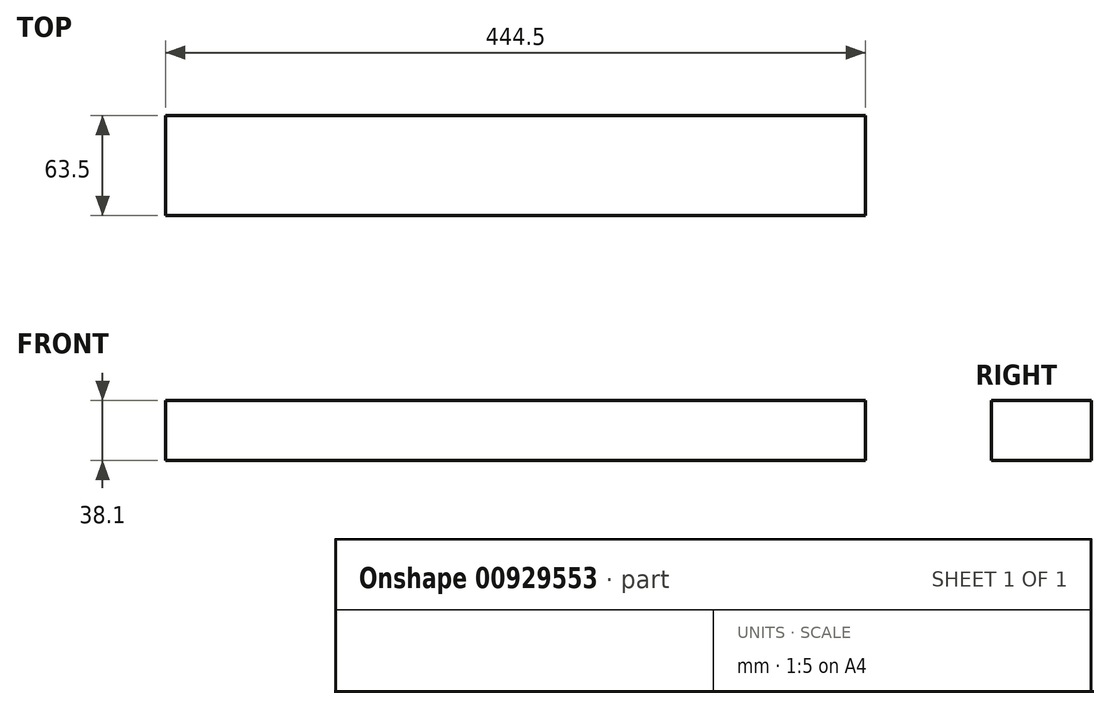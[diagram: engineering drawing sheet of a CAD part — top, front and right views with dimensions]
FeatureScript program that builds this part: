
annotation { "Feature Type Name" : "Feature", "Feature Type Description" : "" }
export const myFeature = defineFeature(function(context is Context, id is Id, definition is map)
    precondition{}
    {
        {
            var Q0;
            Q0=qCreatedBy(makeId("Right.planeOp"),FACE);
            var sketch = newSketch(context, id + "F0", { "sketchPlane" : qUnion([Q0])});
            skLineSegment(sketch, "E0.bottom", {"start": v(31.75, -19.05) * mm, "end": v(-31.75, -19.05) * mm});
            skLineSegment(sketch, "E0.top", {"start": v(31.75, 19.05) * mm, "end": v(-31.75, 19.05) * mm});
            skLineSegment(sketch, "E0.left", {"start": v(31.75, -19.05) * mm, "end": v(31.75, 19.05) * mm});
            skLineSegment(sketch, "E0.right", {"start": v(-31.75, -19.05) * mm, "end": v(-31.75, 19.05) * mm});
            skPoint(sketch, "E0.middle", {"position": v(0, 0) * mm});
            skSolve(sketch);
        }
        {
            var Q0;
            Q0=qSketchRegion(id+"F0",true);
            extrude(context, id + "F1", {"entities" : qUnion([Q0]), "endBound" : BoundingType.SYMMETRIC, "depth" : 444.5 * mm, "offsetDistance" : 25.4 * mm});
        }
    });
